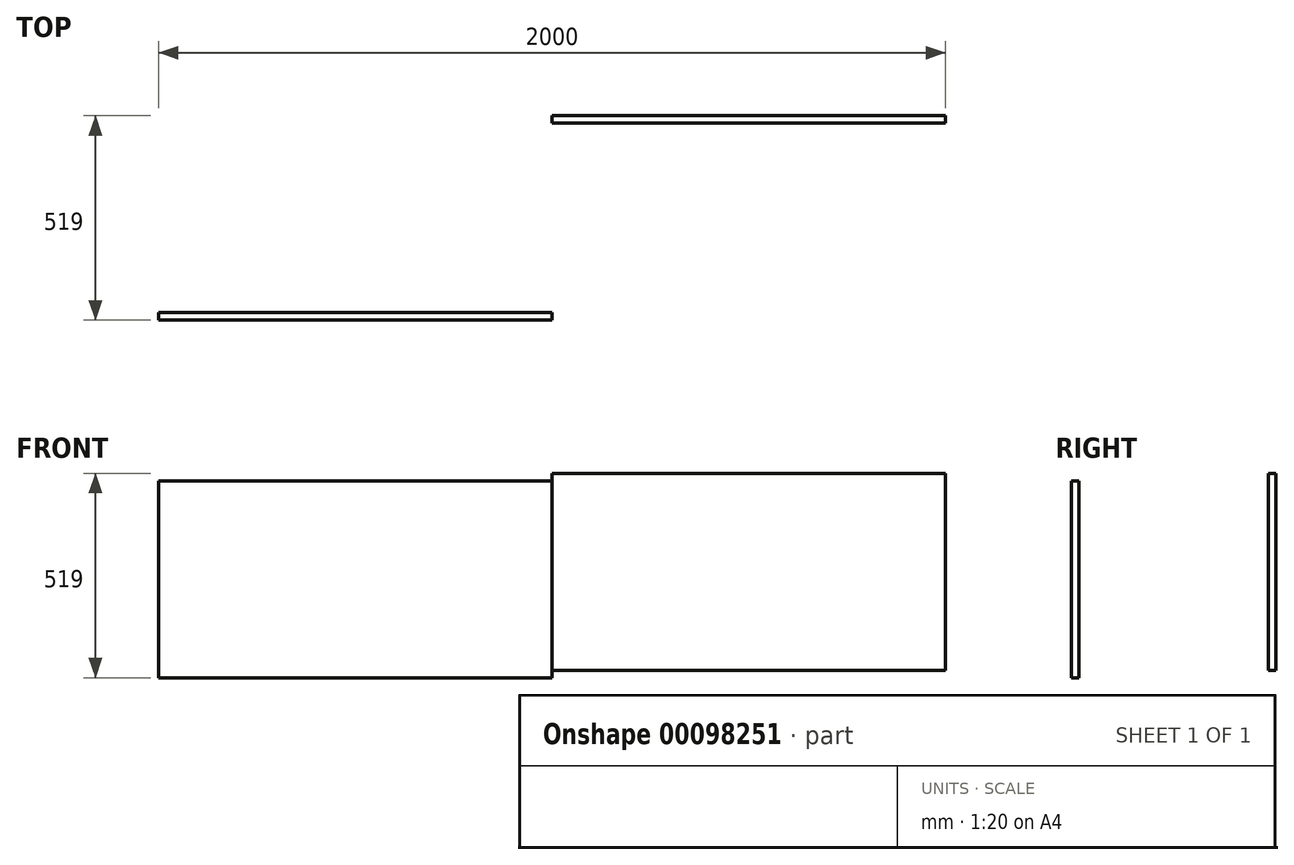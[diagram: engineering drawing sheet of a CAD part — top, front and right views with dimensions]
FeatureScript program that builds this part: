
annotation { "Feature Type Name" : "Feature", "Feature Type Description" : "" }
export const myFeature = defineFeature(function(context is Context, id is Id, definition is map)
    precondition{}
    {
        {
            var Q0;
            Q0=qCreatedBy(makeId("Front.planeOp"),FACE);
            var sketch = newSketch(context, id + "F0", { "sketchPlane" : qUnion([Q0])});
            skLineSegment(sketch, "E0.bottom", {"start": v(500, 250) * mm, "end": v(-500, 250) * mm});
            skLineSegment(sketch, "E0.top", {"start": v(500, -250) * mm, "end": v(-500, -250) * mm});
            skLineSegment(sketch, "E0.left", {"start": v(500, 250) * mm, "end": v(500, -250) * mm});
            skLineSegment(sketch, "E0.right", {"start": v(-500, 250) * mm, "end": v(-500, -250) * mm});
            skPoint(sketch, "E0.middle", {"position": v(0, 0) * mm});
            skSolve(sketch);
        }
        {
            var Q0;
            Q0 = qSketchRegion(id + "F0", true);
            extrude(context, id + "F1", {"entities" : qUnion([Q0]), "endBound" : BoundingType.SYMMETRIC, "depth" : 19 * mm});
        }
        {
            var Q0;
            Q0=makeQuery(id+"F1.opExtrude","SWEPT_BODY",BODY,{"disambiguationData":[OSD([sQuery(id+"F0.wireOp",EDGE,"E0.bottom"),sQuery(id+"F0.wireOp",EDGE,"E0.top"),sQuery(id+"F0.wireOp",EDGE,"E0.left"),sQuery(id+"F0.wireOp",EDGE,"E0.right")])]});
            transform(context, id + "F2", {"entities" : qUnion([Q0]), "transformType" : TransformType.TRANSLATION_3D, "dx" : 1000 * mm, "dy" : 500 * mm, "dz" : 19 * mm, "makeCopy" : true});
        }
    });
